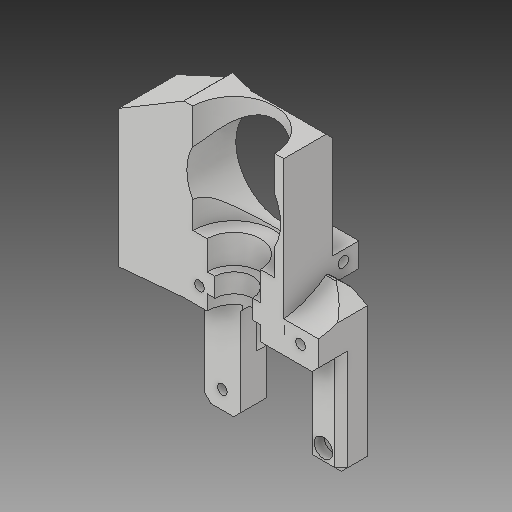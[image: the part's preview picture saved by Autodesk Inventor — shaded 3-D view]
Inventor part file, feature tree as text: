
AUTODESK INVENTOR PART (.ipt)
format: ipt  version: 2018 (Build 220112000, 112)  size: 265,216 bytes
history: native  units: mm
features: other x2, extrude x1
ambient origin geometry x8: Origin, YZ Plane, XZ Plane, XY Plane, X Axis, Y Axis, Z Axis, Center Point
bodies: Solid1 (feature_tree)
feature tree (3):
  extrude  "Extruder Body.ipt"  Depth=10.0mm
  other  "Solid3::Extruder Body.ipt"
  other  "TaggingFeature1"
